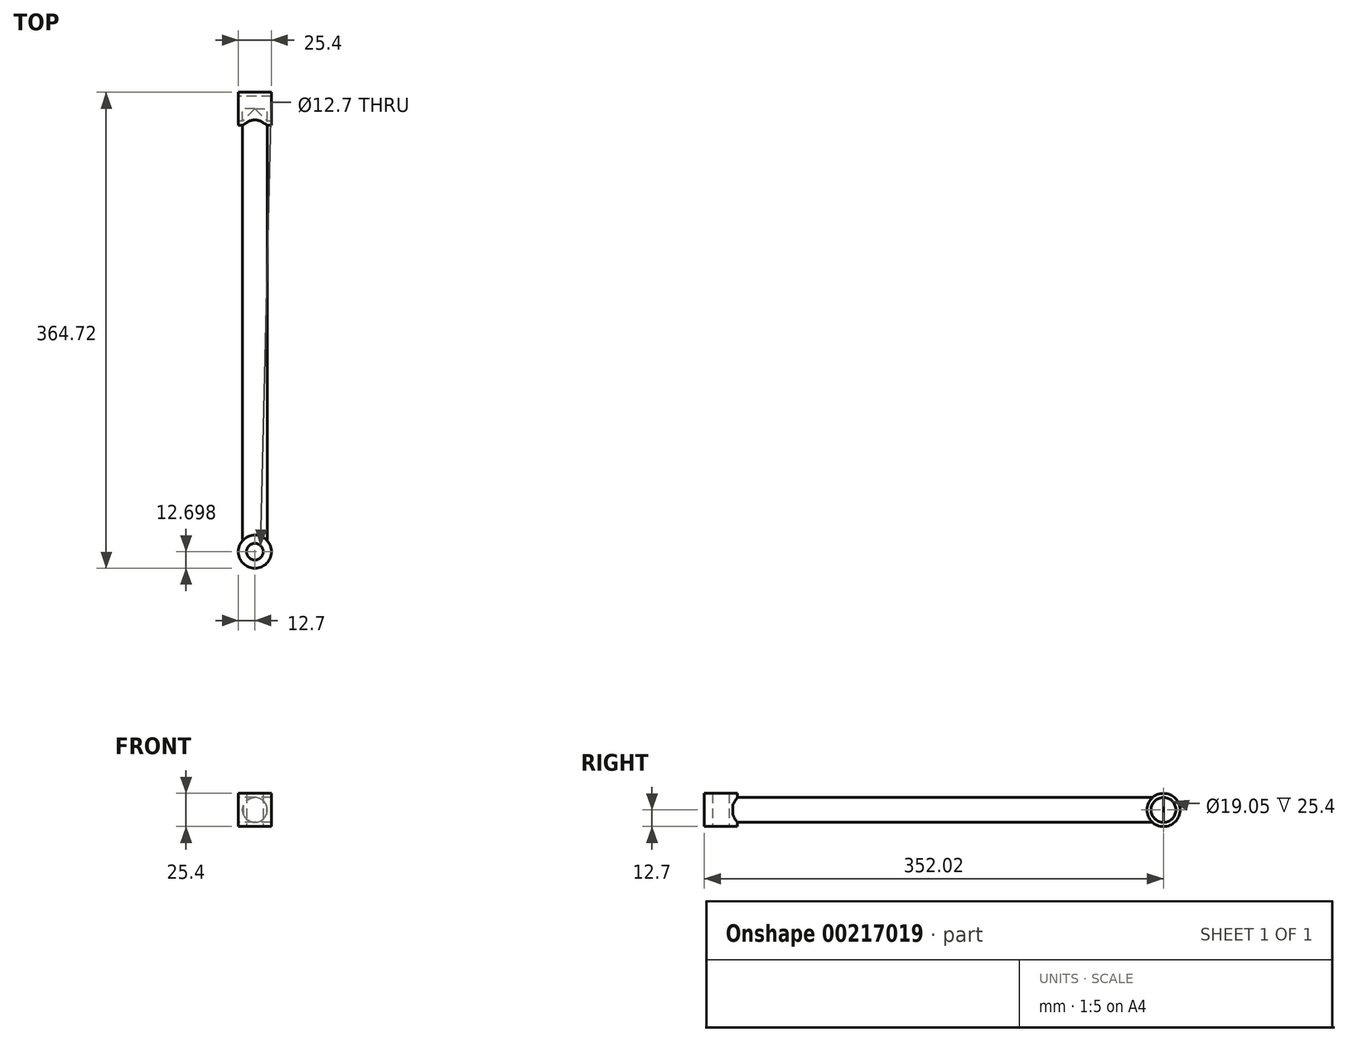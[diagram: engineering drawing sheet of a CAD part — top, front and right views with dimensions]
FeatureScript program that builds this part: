
annotation { "Feature Type Name" : "Feature", "Feature Type Description" : "" }
export const myFeature = defineFeature(function(context is Context, id is Id, definition is map)
    precondition{}
    {
        {
            var Q0;
            Q0=qCreatedBy(makeId("Front.planeOp"),FACE);
            var sketch = newSketch(context, id + "F0", { "sketchPlane" : qUnion([Q0])});
            skCircle(sketch, "E0", {"center": v(0, 0) * mm, "radius": 9.53 * mm});
            skSolve(sketch);
        }
        {
            var Q0;
            Q0=qCreatedBy(makeId("Right.planeOp"),FACE);
            var sketch = newSketch(context, id + "F1", { "sketchPlane" : qUnion([Q0])});
            skCircle(sketch, "E1", {"center": v(0, 0) * mm, "radius": 9.53 * mm});
            skCircle(sketch, "E2", {"center": v(0, 0) * mm, "radius": 12.7 * mm});
            skSolve(sketch);
        }
        {
            var Q0;
            Q0=makeQuery(id+"F1.imprint","IMPRINT",FACE,{"disambiguationData":[TD([[makeQuery(id+"F1.imprint","IMPRINT",EDGE,{"derivedFrom":sQuery(id+"F1.wireOp",EDGE,"E1")}),-1.0]])]});
            extrude(context, id + "F2", {"entities" : qUnion([Q0]), "depth" : 25.4 * mm, "symmetric" : true});
        }
        {
            var Q0;
            Q0=makeQuery(id+"F0.imprint","IMPRINT",FACE,{"disambiguationData":[TD([[makeQuery(id+"F0.imprint","IMPRINT",EDGE,{"derivedFrom":sQuery(id+"F0.wireOp",EDGE,"E0")}),1.0]])]});
            extrude(context, id + "F3", {"entities" : qUnion([Q0]), "operationType" : NewBodyOperationType.ADD, "depth" : 330.2 * mm});
        }
        {
            var Q0;
            Q0=qCreatedBy(makeId("Top.planeOp"),FACE);
            var sketch = newSketch(context, id + "F4", { "sketchPlane" : qUnion([Q0])});
            skCircle(sketch, "E3", {"center": v(0, -339.32) * mm, "radius": 12.7 * mm});
            skCircle(sketch, "E4", {"center": v(0, -339.32) * mm, "radius": 6.35 * mm});
            skSolve(sketch);
        }
        {
            var Q0;
            Q0 = qSketchRegion(id + "F4", true);
            extrude(context, id + "F5", {"entities" : qUnion([Q0]), "operationType" : NewBodyOperationType.ADD, "depth" : 25.4 * mm, "symmetric" : true});
        }
    });
